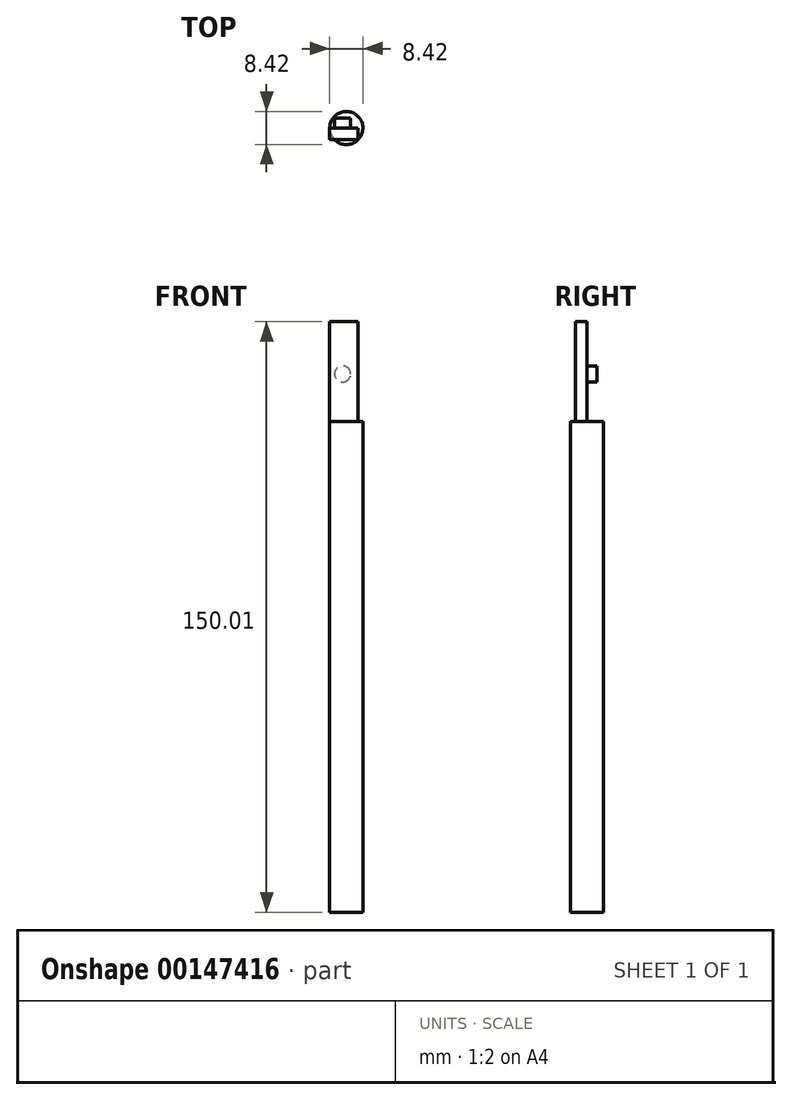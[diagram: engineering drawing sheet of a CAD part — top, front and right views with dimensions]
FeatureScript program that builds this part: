
annotation { "Feature Type Name" : "Feature", "Feature Type Description" : "" }
export const myFeature = defineFeature(function(context is Context, id is Id, definition is map)
    precondition{}
    {
        {
            var Q0;
            Q0=qCreatedBy(makeId("Top.planeOp"),FACE);
            var sketch = newSketch(context, id + "F0", { "sketchPlane" : qUnion([Q0])});
            skCircle(sketch, "E0", {"center": v(0, 0) * mm, "radius": 4.2 * mm});
            skSolve(sketch);
        }
        {
            var Q0;
            Q0=makeQuery(id+"F0.imprint","IMPRINT",FACE,{"disambiguationData":[TD([[makeQuery(id+"F0.imprint","IMPRINT",EDGE,{"derivedFrom":sQuery(id+"F0.wireOp",EDGE,"E0")}),1.0]])]});
            var Q1;
            Q1=sQuery(id+"F0.wireOp",EDGE,"E0");
            extrude(context, id + "F1", {"entities" : qUnion([Q0]), "surfaceEntities" : qUnion([Q1]), "depth" : 124.61 * mm});
        }
        {
            var Q0;
            Q0=makeQuery(id+"F1.opExtrude","CAP_FACE",FACE,{"disambiguationData":[OSD([sQuery(id+"F0.wireOp",EDGE,"E0")])],"isStart":false});
            var sketch = newSketch(context, id + "F2", { "sketchPlane" : qUnion([Q0])});
            skLineSegment(sketch, "E1.bottom", {"start": v(-4.2, 0) * mm, "end": v(2.95, 0) * mm});
            skLineSegment(sketch, "E1.top", {"start": v(-4.2, -3) * mm, "end": v(2.95, -3) * mm});
            skLineSegment(sketch, "E1.left", {"start": v(-4.2, 0) * mm, "end": v(-4.2, -3) * mm});
            skLineSegment(sketch, "E1.right", {"start": v(2.95, 0) * mm, "end": v(2.95, -3) * mm});
            skSolve(sketch);
        }
        {
            var Q0;
            Q0 = qSketchRegion(id + "F2", true);
            extrude(context, id + "F3", {"entities" : qUnion([Q0]), "operationType" : NewBodyOperationType.ADD, "depth" : 25.4 * mm});
        }
        {
            var Q0;
            Q0=makeQuery(id+"F3.opExtrude","SWEPT_FACE",FACE,{"disambiguationData":[OSD([sQuery(id+"F2.wireOp",EDGE,"E1.bottom")])]});
            var sketch = newSketch(context, id + "F4", { "sketchPlane" : qUnion([Q0])});
            skCircle(sketch, "E2", {"center": v(0.94, 136.74) * mm, "radius": 2.04 * mm});
            skSolve(sketch);
        }
        {
            var Q0;
            Q0 = qSketchRegion(id + "F4", true);
            extrude(context, id + "F5", {"entities" : qUnion([Q0]), "operationType" : NewBodyOperationType.ADD, "depth" : 2.54 * mm});
        }
    });
